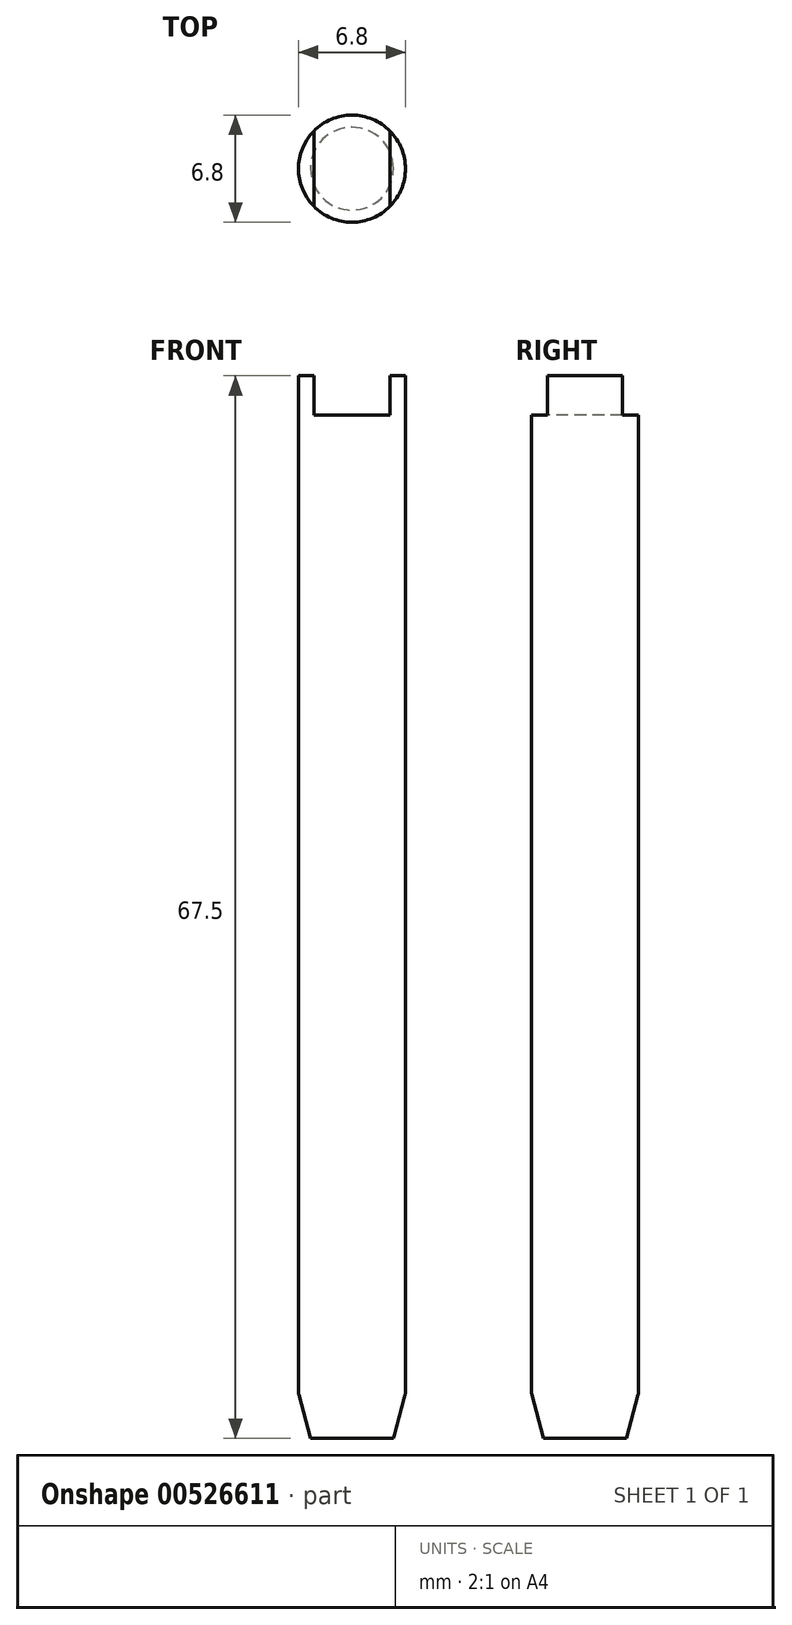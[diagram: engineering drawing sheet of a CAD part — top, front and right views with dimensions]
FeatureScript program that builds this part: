
annotation { "Feature Type Name" : "Feature", "Feature Type Description" : "" }
export const myFeature = defineFeature(function(context is Context, id is Id, definition is map)
    precondition{}
    {
        {
            var Q0;
            Q0=qCreatedBy(makeId("Front.planeOp"),FACE);
            var sketch = newSketch(context, id + "F0", { "sketchPlane" : qUnion([Q0])});
            skLineSegment(sketch, "E0", {"start": v(0, 0) * mm, "end": v(0, -67.5) * mm});
            skLineSegment(sketch, "E1", {"start": v(0, 0) * mm, "end": v(3.4, 0) * mm});
            skLineSegment(sketch, "E2", {"start": v(0, -67.5) * mm, "end": v(2.63, -67.5) * mm});
            skLineSegment(sketch, "E3", {"start": v(2.63, -67.5) * mm, "end": v(3.37, -64.73) * mm});
            skLineSegment(sketch, "E4", {"start": v(3.4, 0) * mm, "end": v(3.4, -64.52) * mm});
            skPoint(sketch, "E5.visualSharp", {"position": v(3.4, -64.63) * mm});
            skArc(sketch, "E5.filletArc", {"start": v(3.37, -64.73) * mm, "mid": v(3.4, -64.63) * mm, "end": v(3.4, -64.52) * mm});
            skSolve(sketch);
        }
        {
            var Q0;
            Q0=makeQuery(id+"F0.imprint","IMPRINT",FACE,{"disambiguationData":[TD([[makeQuery(id+"F0.imprint","IMPRINT",EDGE,{"derivedFrom":sQuery(id+"F0.wireOp",EDGE,"E0")}),1.0]])]});
            var Q1;
            Q1=sQuery(id+"F0.wireOp",EDGE,"E0");
            revolve(context, id + "F1", {"entities" : qUnion([Q0]), "axis" : qUnion([Q1]), "revolveType" : RevolveType.FULL});
        }
        {
            var Q0;
            Q0=qCreatedBy(makeId("Front.planeOp"),FACE);
            var sketch = newSketch(context, id + "F2", { "sketchPlane" : qUnion([Q0])});
            skLineSegment(sketch, "E6.bottom", {"start": v(2.42, -2.5) * mm, "end": v(-2.43, -2.5) * mm});
            skLineSegment(sketch, "E6.top", {"start": v(2.43, 2.5) * mm, "end": v(-2.43, 2.5) * mm});
            skLineSegment(sketch, "E6.left", {"start": v(2.42, -2.5) * mm, "end": v(2.42, 2.5) * mm});
            skLineSegment(sketch, "E6.right", {"start": v(-2.43, -2.5) * mm, "end": v(-2.43, 2.5) * mm});
            skPoint(sketch, "E6.middle", {"position": v(0, 0) * mm});
            skSolve(sketch);
        }
        {
            var Q0;
            Q0 = qSketchRegion(id + "F2", true);
            extrude(context, id + "F3", {"entities" : qUnion([Q0]), "operationType" : NewBodyOperationType.REMOVE, "endBound" : BoundingType.SYMMETRIC, "oppositeDirection" : true, "depth" : 25.4 * mm, "offsetDistance" : 25.4 * mm});
        }
    });
